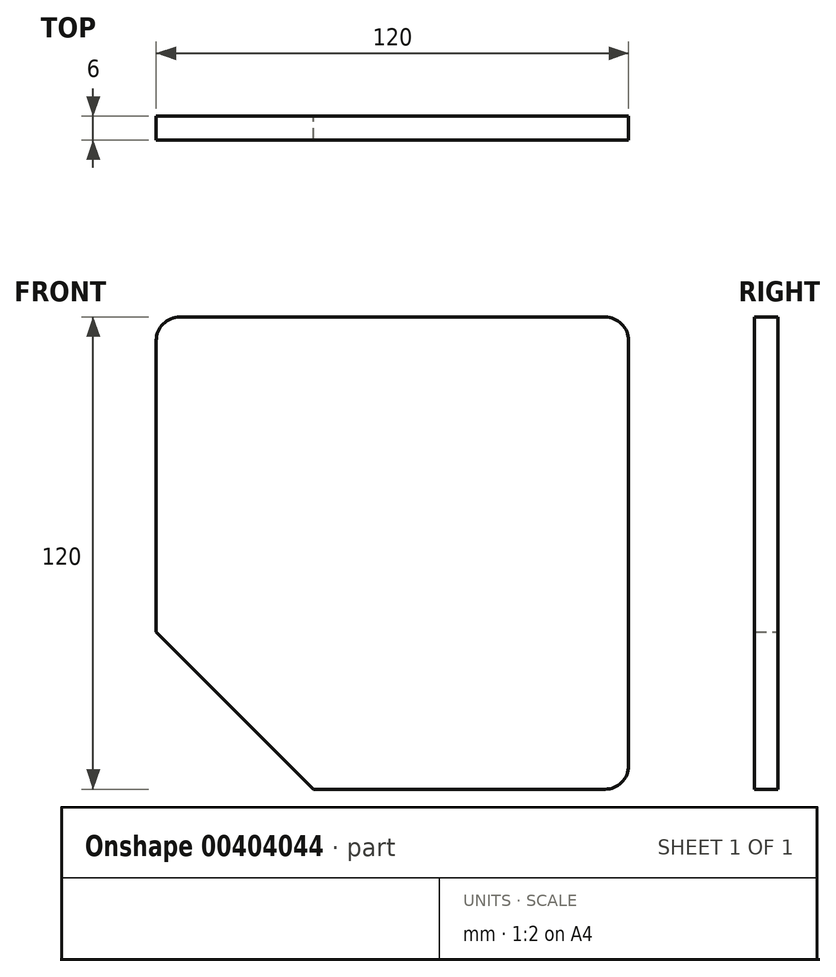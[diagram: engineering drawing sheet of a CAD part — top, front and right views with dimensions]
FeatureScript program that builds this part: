
annotation { "Feature Type Name" : "Feature", "Feature Type Description" : "" }
export const myFeature = defineFeature(function(context is Context, id is Id, definition is map)
    precondition{}
    {
        {
            var Q0;
            Q0=qCreatedBy(makeId("Front.planeOp"),FACE);
            var sketch = newSketch(context, id + "F0", { "sketchPlane" : qUnion([Q0])});
            skLineSegment(sketch, "E0", {"start": v(0, 0) * mm, "end": v(-120, 0) * mm});
            skLineSegment(sketch, "E1", {"start": v(-120, 0) * mm, "end": v(-120, -80) * mm});
            skLineSegment(sketch, "E2", {"start": v(-120, -80) * mm, "end": v(-80, -120) * mm});
            skLineSegment(sketch, "E3", {"start": v(-80, -120) * mm, "end": v(0, -120) * mm});
            skLineSegment(sketch, "E4", {"start": v(0, -120) * mm, "end": v(0, 0) * mm});
            skSolve(sketch);
        }
        {
            var Q0;
            Q0=makeQuery(id+"F0.imprint","IMPRINT",FACE,{"disambiguationData":[TD([[makeQuery(id+"F0.imprint","IMPRINT",EDGE,{"derivedFrom":sQuery(id+"F0.wireOp",EDGE,"E0")}),1.0]])]});
            extrude(context, id + "F1", {"entities" : qUnion([Q0]), "depth" : 6 * mm});
        }
        {
            var Q0;
            Q0=makeQuery(id+"F1.opExtrude","SWEPT_EDGE",EDGE,{"disambiguationData":[OSD([sQuery(id+"F0.wireOp",EDGE,"E0"),sQuery(id+"F0.wireOp",EDGE,"E4")])]});
            fillet(context, id + "F2", {"entities" : qUnion([Q0]), "radius" : 6 * mm, "tangentPropagation" : true, "allowEdgeOverflow" : false});
        }
        {
            var Q0;
            Q0=makeQuery(id+"F1.opExtrude","SWEPT_EDGE",EDGE,{"disambiguationData":[OSD([sQuery(id+"F0.wireOp",EDGE,"E0"),sQuery(id+"F0.wireOp",EDGE,"E1")])]});
            var Q1;
            Q1=makeQuery(id+"F1.opExtrude","SWEPT_EDGE",EDGE,{"disambiguationData":[OSD([sQuery(id+"F0.wireOp",EDGE,"E3"),sQuery(id+"F0.wireOp",EDGE,"E4")])]});
            fillet(context, id + "F3", {"entities" : qUnion([Q0, Q1]), "radius" : 6 * mm, "tangentPropagation" : true, "allowEdgeOverflow" : false});
        }
    });
